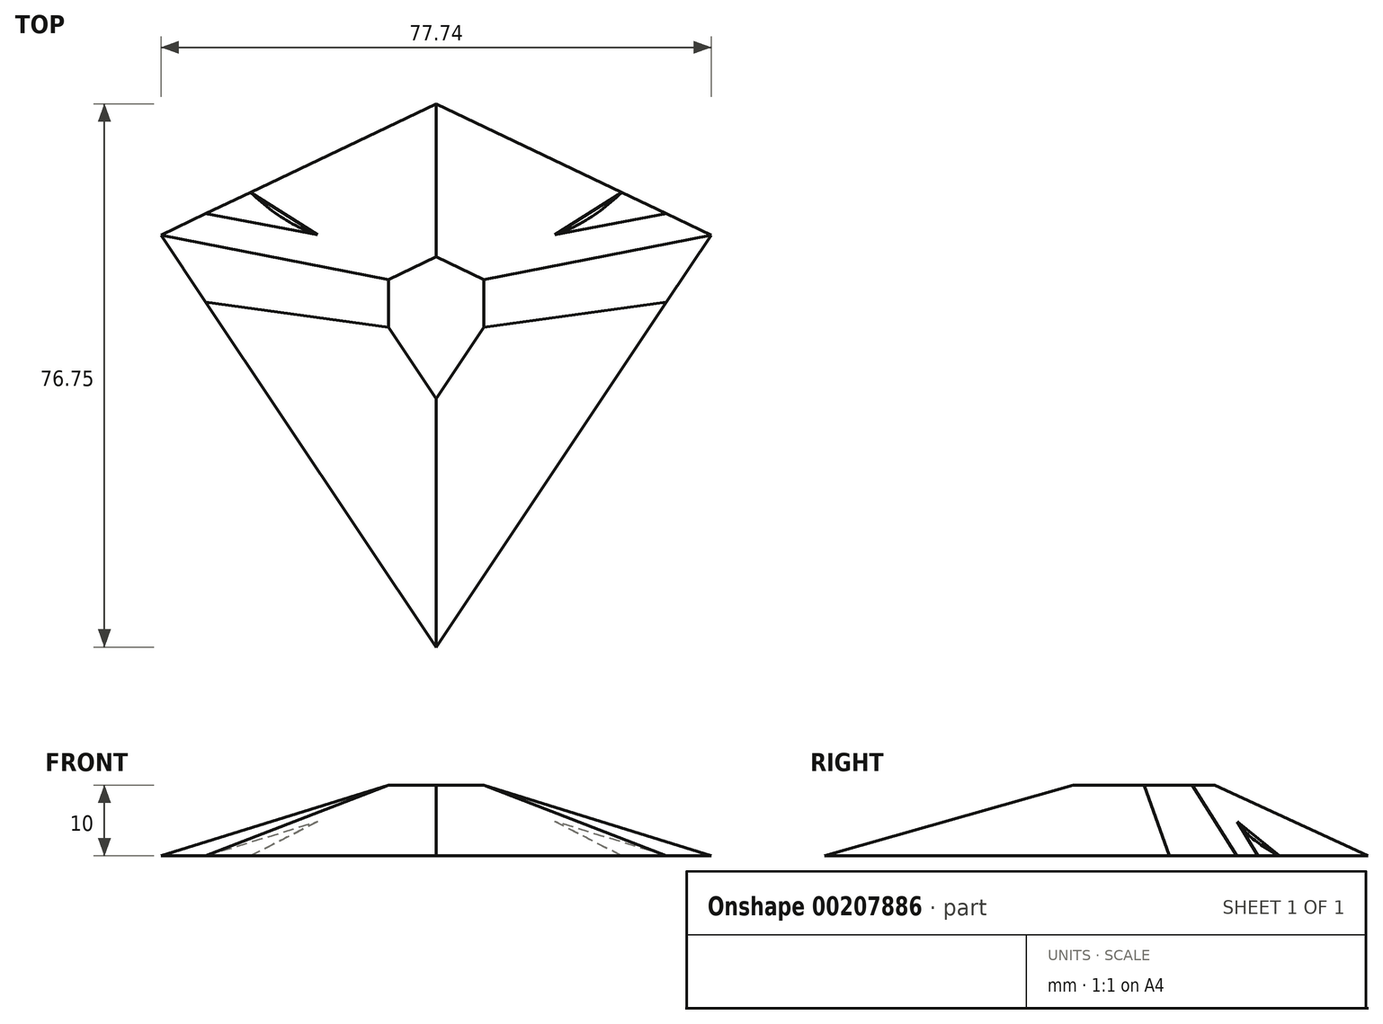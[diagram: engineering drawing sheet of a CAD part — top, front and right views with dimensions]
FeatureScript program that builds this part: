
annotation { "Feature Type Name" : "Feature", "Feature Type Description" : "" }
export const myFeature = defineFeature(function(context is Context, id is Id, definition is map)
    precondition{}
    {
        {
            var Q0;
            Q0=qCreatedBy(makeId("Top.planeOp"),FACE);
            var sketch = newSketch(context, id + "F0", { "sketchPlane" : qUnion([Q0])});
            skLineSegment(sketch, "E0", {"start": v(-38.87, 58.21) * mm, "end": v(0, 0) * mm});
            skLineSegment(sketch, "E1", {"start": v(0, 0) * mm, "end": v(0, 0) * mm});
            skLineSegment(sketch, "E2", {"start": v(0, 0) * mm, "end": v(38.87, 58.21) * mm});
            skLineSegment(sketch, "E3", {"start": v(-38.87, 58.21) * mm, "end": v(0, 76.75) * mm});
            skLineSegment(sketch, "E4", {"start": v(0, 76.75) * mm, "end": v(38.87, 58.21) * mm});
            skLineSegment(sketch, "E5", {"start": v(-26.21, 39.25) * mm, "end": v(-26.21, 64.25) * mm});
            skLineSegment(sketch, "E6", {"start": v(26.21, 39.25) * mm, "end": v(26.21, 64.25) * mm});
            skSolve(sketch);
        }
        {
            var Q0;
            {var subQ4=sQuery(id+"F0.wireOp",EDGE,"E5");Q0=makeQuery(id+"F0.imprint","IMPRINT",FACE,{"disambiguationData":[TD([[makeQuery(id+"F0.imprint","IMPRINT",EDGE,{"derivedFrom":subQ4}),-1.0]])]});}
            cPlane(context, id + "F1", {"entities" : qUnion([Q0]), "cplaneType" : CPlaneType.OFFSET, "offset" : 10 * mm, "width" : 150 * mm, "height" : 150 * mm});
        }
        {
            var Q0;
            Q0=qCreatedBy(id+"F1.planeOp",FACE);
            var sketch = newSketch(context, id + "F2", { "sketchPlane" : qUnion([Q0])});
            skLineSegment(sketch, "E7.0", {"start": v(6.71, 45.16) * mm, "end": v(6.71, 51.94) * mm});
            skLineSegment(sketch, "E7.1", {"start": v(0, 55.14) * mm, "end": v(-6.71, 51.94) * mm});
            skLineSegment(sketch, "E7.2", {"start": v(-6.71, 51.94) * mm, "end": v(-6.71, 45.16) * mm});
            skLineSegment(sketch, "E7.3", {"start": v(6.71, 51.94) * mm, "end": v(0, 55.14) * mm});
            skLineSegment(sketch, "E7.4", {"start": v(-6.71, 45.16) * mm, "end": v(0, 35.11) * mm});
            skLineSegment(sketch, "E7.5", {"start": v(0, 35.11) * mm, "end": v(6.71, 45.16) * mm});
            skSolve(sketch);
        }
        {
            var Q0;
            {var subQ4=sQuery(id+"F0.wireOp",EDGE,"E5");Q0=makeQuery(id+"F0.imprint","IMPRINT",FACE,{"disambiguationData":[TD([[makeQuery(id+"F0.imprint","IMPRINT",EDGE,{"derivedFrom":subQ4}),-1.0]])]});}
            var Q1;
            Q1=makeQuery(id+"F2.imprint","IMPRINT",FACE,{"disambiguationData":[TD([[makeQuery(id+"F2.imprint","IMPRINT",EDGE,{"derivedFrom":sQuery(id+"F2.wireOp",EDGE,"E7.0")}),1.0]])]});
            loft(context, id + "F3", {"sheetProfilesArray" : [{ "sheetProfileEntities" : qUnion([Q0]) }, { "sheetProfileEntities" : qUnion([Q1]) }]});
        }
        {
            var Q1;
            {var subQ3=sQuery(id+"F0.wireOp",EDGE,"E5");Q1=makeQuery(id+"F0.imprint","IMPRINT",FACE,{"disambiguationData":[TD([[makeQuery(id+"F0.imprint","IMPRINT",EDGE,{"derivedFrom":subQ3}),1.0]])]});}
            var Q2;
            Q2=makeQuery(id+"F3.opLoft","CAP_FACE",FACE,{"disambiguationData":[OSD([makeQuery(id+"F2.imprint","IMPRINT",FACE,{"disambiguationData":[TD([[makeQuery(id+"F2.imprint","IMPRINT",EDGE,{"derivedFrom":sQuery(id+"F2.wireOp",EDGE,"E7.0")}),1.0]])]})])],"isStart":true});
            loft(context, id + "F4", {"operationType" : NewBodyOperationType.ADD, "sheetProfilesArray" : [{ "sheetProfileEntities" : qUnion([Q1]) }, { "sheetProfileEntities" : qUnion([Q2]) }]});
        }
        {
            var Q1;
            {var subQ3=sQuery(id+"F0.wireOp",EDGE,"E6");Q1=makeQuery(id+"F0.imprint","IMPRINT",FACE,{"disambiguationData":[TD([[makeQuery(id+"F0.imprint","IMPRINT",EDGE,{"derivedFrom":subQ3}),-1.0]])]});}
            var Q2;
            Q2=makeQuery(id+"F3.opLoft","CAP_FACE",FACE,{"disambiguationData":[OSD([makeQuery(id+"F2.imprint","IMPRINT",FACE,{"disambiguationData":[TD([[makeQuery(id+"F2.imprint","IMPRINT",EDGE,{"derivedFrom":sQuery(id+"F2.wireOp",EDGE,"E7.0")}),1.0]])]})])],"isStart":true});
            loft(context, id + "F5", {"operationType" : NewBodyOperationType.ADD, "sheetProfilesArray" : [{ "sheetProfileEntities" : qUnion([Q1]) }, { "sheetProfileEntities" : qUnion([Q2]) }]});
        }
    });
